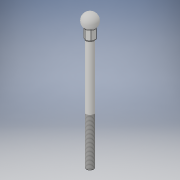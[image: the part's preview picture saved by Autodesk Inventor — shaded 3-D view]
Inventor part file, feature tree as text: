
AUTODESK INVENTOR PART (.ipt)
format: ipt  version: 2018 (Build 220112000, 112)  size: 241,664 bytes
history: native  units: mm
features: fillet x3, sketch x2, revolve x1, plane x1, extrude x1, thread x1, chamfer x1
ambient origin geometry x8: Origin, YZ Plane, XZ Plane, XY Plane, X Axis, Y Axis, Z Axis, Center Point
bodies: Solid1 (feature_tree)
feature tree (10):
  revolve  "Revolution1"  [1 undecoded]
  plane  "Work Plane1"
  extrude  "Extrusion1"  Depth=0.25mm
  fillet  "Fillet1"  [1 undecoded]
  fillet  "Fillet2"  [1 undecoded]
  fillet  "Fillet3"  Radius=3.0mm
  thread  "Thread1"  [1 undecoded]
  chamfer  "Chamfer1"  Distance=0.25mm
  sketch  "Sketch1"  dims[d0=5.0mm d1=40.0mm]
  sketch  "Sketch2"  dims[d2=1.25mm d3=0.25mm d4=90.0deg d5=-35.0mm d6=3.0mm d7=10.0mm d8=0.0mm d9=0.25mm d10=0.25mm d11=0.25mm d12=15.0mm d13=0.0mm d14=0.25mm d15=2.0mm d16=45.0deg]
note: 4 required parameter values undecoded (feature->parameter linkage not recoverable at this tier; creation-order binding heuristic only, values carry confidence <= 0.55)